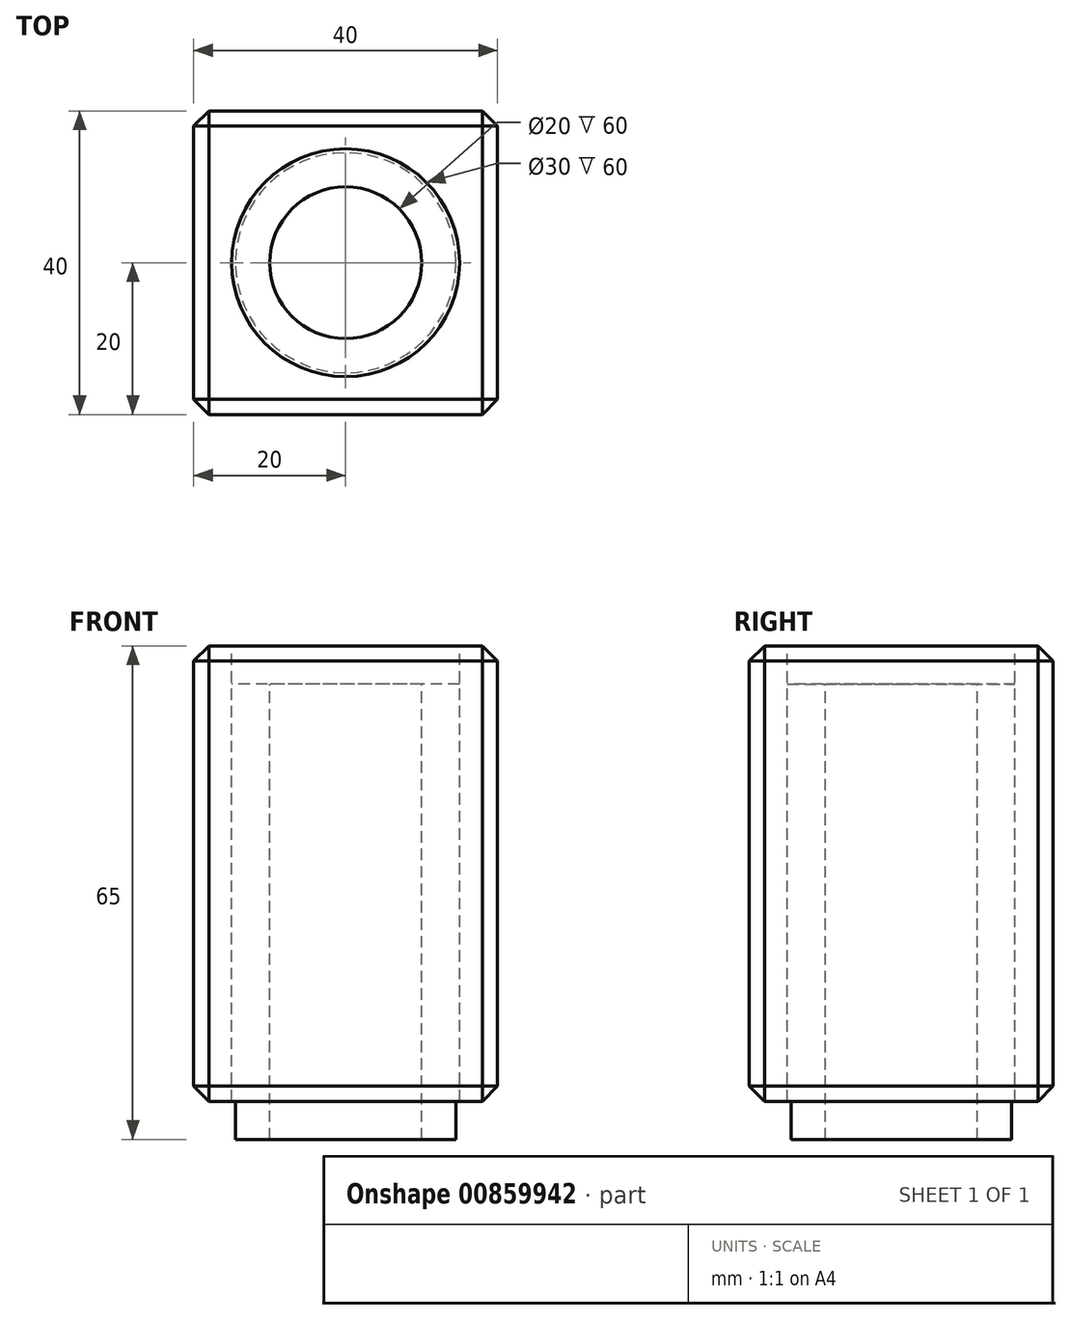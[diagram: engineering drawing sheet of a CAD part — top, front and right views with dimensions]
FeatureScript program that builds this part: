
annotation { "Feature Type Name" : "Feature", "Feature Type Description" : "" }
export const myFeature = defineFeature(function(context is Context, id is Id, definition is map)
    precondition{}
    {
        {
            var Q0;
            Q0=qCreatedBy(makeId("Top.planeOp"),FACE);
            var sketch = newSketch(context, id + "F0", { "sketchPlane" : qUnion([Q0])});
            skLineSegment(sketch, "E0.bottom", {"start": v(-20, 20) * mm, "end": v(20, 20) * mm});
            skLineSegment(sketch, "E0.top", {"start": v(-20, -20) * mm, "end": v(20, -20) * mm});
            skLineSegment(sketch, "E0.left", {"start": v(-20, 20) * mm, "end": v(-20, -20) * mm});
            skLineSegment(sketch, "E0.right", {"start": v(20, 20) * mm, "end": v(20, -20) * mm});
            skSolve(sketch);
        }
        {
            var Q0;
            Q0 = qSketchRegion(id + "F0", true);
            extrude(context, id + "F1", {"entities" : qUnion([Q0]), "depth" : 60 * mm, "offsetDistance" : 25 * mm});
        }
        {
            var Q0;
            Q0=makeQuery(id+"F1.opExtrude","CAP_FACE",FACE,{"disambiguationData":[OSD([sQuery(id+"F0.wireOp",EDGE,"E0.bottom"),sQuery(id+"F0.wireOp",EDGE,"E0.top"),sQuery(id+"F0.wireOp",EDGE,"E0.left"),sQuery(id+"F0.wireOp",EDGE,"E0.right")])],"isStart":false});
            var sketch = newSketch(context, id + "F2", { "sketchPlane" : qUnion([Q0])});
            skCircle(sketch, "E1", {"center": v(0, 0) * mm, "radius": 15 * mm});
            skSolve(sketch);
        }
        {
            var Q0;
            Q0=makeQuery(id+"F2.imprint","IMPRINT",FACE,{"disambiguationData":[TD([[makeQuery(id+"F2.imprint","IMPRINT",EDGE,{"derivedFrom":sQuery(id+"F2.wireOp",EDGE,"E1")}),1.0]])]});
            extrude(context, id + "F3", {"entities" : qUnion([Q0]), "operationType" : NewBodyOperationType.REMOVE, "oppositeDirection" : true, "depth" : 60 * mm, "offsetDistance" : 25 * mm});
        }
        {
            var Q0;
            Q0=makeQuery(id+"F1.opExtrude","CAP_FACE",FACE,{"disambiguationData":[OSD([sQuery(id+"F0.wireOp",EDGE,"E0.bottom"),sQuery(id+"F0.wireOp",EDGE,"E0.top"),sQuery(id+"F0.wireOp",EDGE,"E0.left"),sQuery(id+"F0.wireOp",EDGE,"E0.right")])],"isStart":false});
            var sketch = newSketch(context, id + "F4", { "sketchPlane" : qUnion([Q0])});
            skCircle(sketch, "E2", {"center": v(0, 0) * mm, "radius": 15 * mm});
            skCircle(sketch, "E3", {"center": v(0, 0) * mm, "radius": 10 * mm});
            skSolve(sketch);
        }
        {
            var Q0;
            Q0=makeQuery(id+"F4.imprint","IMPRINT",FACE,{"disambiguationData":[TD([[makeQuery(id+"F4.imprint","IMPRINT",EDGE,{"derivedFrom":sQuery(id+"F4.wireOp",EDGE,"E2")}),1.0]])]});
            extrude(context, id + "F5", {"entities" : qUnion([Q0]), "oppositeDirection" : true, "depth" : 65 * mm, "offsetDistance" : 25 * mm, "hasSecondDirection" : true, "secondDirectionOppositeDirection" : true, "secondDirectionDepth" : 5 * mm});
        }
        {
            var Q0;
            Q0=makeQuery(id+"F1.opExtrude","SWEPT_EDGE",EDGE,{"disambiguationData":[OSD([sQuery(id+"F0.wireOp",EDGE,"E0.top"),sQuery(id+"F0.wireOp",EDGE,"E0.right")])]});
            var Q1;
            Q1=makeQuery(id+"F1.opExtrude","SWEPT_EDGE",EDGE,{"disambiguationData":[OSD([sQuery(id+"F0.wireOp",EDGE,"E0.bottom"),sQuery(id+"F0.wireOp",EDGE,"E0.right")])]});
            var Q2;
            Q2=makeQuery(id+"F1.opExtrude","SWEPT_EDGE",EDGE,{"disambiguationData":[OSD([sQuery(id+"F0.wireOp",EDGE,"E0.top"),sQuery(id+"F0.wireOp",EDGE,"E0.left")])]});
            var Q3;
            Q3=makeQuery(id+"F1.opExtrude","CAP_EDGE",EDGE,{"disambiguationData":[OSD([sQuery(id+"F0.wireOp",EDGE,"E0.right")])],"isStart":false});
            var Q4;
            Q4=makeQuery(id+"F1.opExtrude","CAP_EDGE",EDGE,{"disambiguationData":[OSD([sQuery(id+"F0.wireOp",EDGE,"E0.top")])],"isStart":false});
            var Q5;
            Q5=makeQuery(id+"F1.opExtrude","CAP_EDGE",EDGE,{"disambiguationData":[OSD([sQuery(id+"F0.wireOp",EDGE,"E0.left")])],"isStart":false});
            var Q6;
            Q6=makeQuery(id+"F1.opExtrude","CAP_EDGE",EDGE,{"disambiguationData":[OSD([sQuery(id+"F0.wireOp",EDGE,"E0.bottom")])],"isStart":false});
            var Q7;
            Q7=makeQuery(id+"F1.opExtrude","SWEPT_EDGE",EDGE,{"disambiguationData":[OSD([sQuery(id+"F0.wireOp",EDGE,"E0.bottom"),sQuery(id+"F0.wireOp",EDGE,"E0.left")])]});
            var Q8;
            Q8=makeQuery(id+"F1.opExtrude","CAP_EDGE",EDGE,{"disambiguationData":[OSD([sQuery(id+"F0.wireOp",EDGE,"E0.right")])],"isStart":true});
            var Q9;
            Q9=makeQuery(id+"F1.opExtrude","CAP_EDGE",EDGE,{"disambiguationData":[OSD([sQuery(id+"F0.wireOp",EDGE,"E0.top")])],"isStart":true});
            var Q10;
            Q10=makeQuery(id+"F1.opExtrude","CAP_EDGE",EDGE,{"disambiguationData":[OSD([sQuery(id+"F0.wireOp",EDGE,"E0.left")])],"isStart":true});
            var Q11;
            Q11=makeQuery(id+"F1.opExtrude","CAP_EDGE",EDGE,{"disambiguationData":[OSD([sQuery(id+"F0.wireOp",EDGE,"E0.bottom")])],"isStart":true});
            chamfer(context, id + "F6", {"entities" : qUnion([Q0, Q1, Q2, Q3, Q4, Q5, Q6, Q7, Q8, Q9, Q10, Q11]), "width" : 2 * mm, "tangentPropagation" : true});
        }
        {
            var Q0;
            Q0=makeQuery(id+"F5.opExtrude","CAP_FACE",FACE,{"disambiguationData":[OSD([sQuery(id+"F4.wireOp",EDGE,"E2"),sQuery(id+"F4.wireOp",EDGE,"E3")])],"isStart":false});
            var sketch = newSketch(context, id + "F7", { "sketchPlane" : qUnion([Q0])});
            skCircle(sketch, "E4", {"center": v(0, 0) * mm, "radius": 14.5 * mm});
            skLineSegment(sketch, "E5.bottom", {"start": v(-44.83, 33.33) * mm, "end": v(43.66, 33.33) * mm});
            skLineSegment(sketch, "E5.top", {"start": v(-44.83, -40.74) * mm, "end": v(43.66, -40.74) * mm});
            skLineSegment(sketch, "E5.left", {"start": v(-44.83, 33.33) * mm, "end": v(-44.83, -40.74) * mm});
            skLineSegment(sketch, "E5.right", {"start": v(43.66, 33.33) * mm, "end": v(43.66, -40.74) * mm});
            skSolve(sketch);
        }
        {
            var Q0;
            Q0 = qSketchRegion(id + "F7", true);
            extrude(context, id + "F8", {"entities" : qUnion([Q0]), "operationType" : NewBodyOperationType.REMOVE, "oppositeDirection" : true, "depth" : 5 * mm, "offsetDistance" : 25 * mm});
        }
    });
